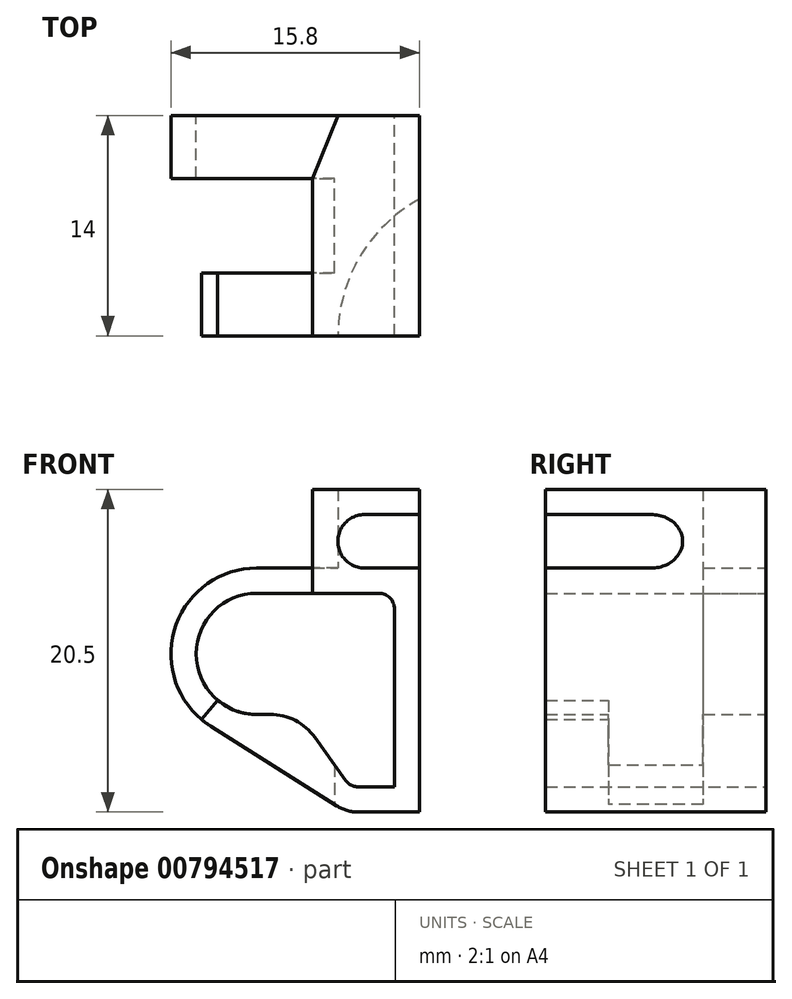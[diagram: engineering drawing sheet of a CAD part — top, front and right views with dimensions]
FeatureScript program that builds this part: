
annotation { "Feature Type Name" : "Feature", "Feature Type Description" : "" }
export const myFeature = defineFeature(function(context is Context, id is Id, definition is map)
    precondition{}
    {
        {
            var Q0;
            Q0=qCreatedBy(makeId("Front.planeOp"),FACE);
            var sketch = newSketch(context, id + "F0", { "sketchPlane" : qUnion([Q0])});
            skLineSegment(sketch, "E0", {"start": v(0, -12.3) * mm, "end": v(0, -1) * mm});
            skLineSegment(sketch, "E1", {"start": v(-1, 0) * mm, "end": v(-8.75, 0) * mm});
            skLineSegment(sketch, "E2", {"start": v(0, -12.3) * mm, "end": v(-2.29, -12.3) * mm});
            skLineSegment(sketch, "E3", {"start": v(-3.1, -11.88) * mm, "end": v(-5.05, -9.16) * mm});
            skLineSegment(sketch, "E4", {"start": v(-7.9, -7.7) * mm, "end": v(-8.75, -7.7) * mm});
            skArc(sketch, "E5", {"start": v(-8.75, 0) * mm, "mid": v(-12.6, -3.85) * mm, "end": v(-8.75, -7.7) * mm});
            skPoint(sketch, "E6.visualSharp", {"position": v(-6.1, -7.7) * mm});
            skArc(sketch, "E6.filletArc", {"start": v(-5.05, -9.16) * mm, "mid": v(-6.3, -8.09) * mm, "end": v(-7.9, -7.7) * mm});
            skPoint(sketch, "E7.visualSharp", {"position": v(-2.8, -12.3) * mm});
            skArc(sketch, "E7.filletArc", {"start": v(-3.1, -11.88) * mm, "mid": v(-2.74, -12.19) * mm, "end": v(-2.29, -12.3) * mm});
            skPoint(sketch, "E8.visualSharp", {"position": v(0, 0) * mm});
            skArc(sketch, "E8.filletArc", {"start": v(0, -1) * mm, "mid": v(-0.3, -0.3) * mm, "end": v(-1, 0) * mm});
            skLineSegment(sketch, "E9.1", {"start": v(1.6, -13.9) * mm, "end": v(1.6, 1.6) * mm});
            skArc(sketch, "E9.2", {"start": v(-8.75, 1.6) * mm, "mid": v(-13.99, -2.34) * mm, "end": v(-11.66, -8.46) * mm});
            skArc(sketch, "E9.4", {"start": v(-3.67, -13.5) * mm, "mid": v(-3, -13.8) * mm, "end": v(-2.29, -13.9) * mm});
            skLineSegment(sketch, "E9.5", {"start": v(1.6, 1.6) * mm, "end": v(-8.75, 1.6) * mm});
            skLineSegment(sketch, "E9.6", {"start": v(1.6, -13.9) * mm, "end": v(-2.29, -13.9) * mm});
            skLineSegment(sketch, "E10", {"start": v(-11.66, -8.46) * mm, "end": v(-3.67, -13.5) * mm});
            skSolve(sketch);
        }
        {
            var Q0;
            Q0=makeQuery(id+"F0.imprint","IMPRINT",FACE,{"disambiguationData":[TD([[makeQuery(id+"F0.imprint","IMPRINT",EDGE,{"derivedFrom":sQuery(id+"F0.wireOp",EDGE,"E0")}),-1.0]])]});
            extrude(context, id + "F1", {"entities" : qUnion([Q0]), "depth" : 14 * mm, "offsetDistance" : 25 * mm});
        }
        {
            var Q0;
            Q0=makeQuery(id+"F1.opExtrude","CAP_FACE",FACE,{"disambiguationData":[OSD([sQuery(id+"F0.wireOp",EDGE,"E0"),sQuery(id+"F0.wireOp",EDGE,"E1"),sQuery(id+"F0.wireOp",EDGE,"E2"),sQuery(id+"F0.wireOp",EDGE,"E3"),sQuery(id+"F0.wireOp",EDGE,"E4"),sQuery(id+"F0.wireOp",EDGE,"E5"),sQuery(id+"F0.wireOp",EDGE,"E6.filletArc"),sQuery(id+"F0.wireOp",EDGE,"E7.filletArc"),sQuery(id+"F0.wireOp",EDGE,"E8.filletArc"),sQuery(id+"F0.wireOp",EDGE,"E9.0"),sQuery(id+"F0.wireOp",EDGE,"E9.1"),sQuery(id+"F0.wireOp",EDGE,"E9.2"),sQuery(id+"F0.wireOp",EDGE,"E9.4"),sQuery(id+"F0.wireOp",EDGE,"E9.5"),sQuery(id+"F0.wireOp",EDGE,"E9.6"),sQuery(id+"F0.wireOp",EDGE,"E10")])],"isStart":false});
            var sketch = newSketch(context, id + "F2", { "sketchPlane" : qUnion([Q0])});
            skLineSegment(sketch, "E11", {"start": v(-5.2, 8.6) * mm, "end": v(-5.2, -3.4) * mm});
            skLineSegment(sketch, "E12", {"start": v(-5.2, -3.4) * mm, "end": v(-3.8, -3.4) * mm});
            skLineSegment(sketch, "E13", {"start": v(-3.8, -3.4) * mm, "end": v(-3.8, -16.4) * mm});
            skLineSegment(sketch, "E14", {"start": v(-3.8, -16.4) * mm, "end": v(-19.2, -16.4) * mm});
            skLineSegment(sketch, "E15", {"start": v(-19.2, -16.4) * mm, "end": v(-19.2, 8.6) * mm});
            skLineSegment(sketch, "E16", {"start": v(-19.2, 8.6) * mm, "end": v(-5.2, 8.6) * mm});
            skSolve(sketch);
        }
        {
            var Q0;
            {var subQ1=sQuery(id+"F2.wireOp",EDGE,"E14");Q0=makeQuery(id+"F2.imprint","IMPRINT",FACE,{"disambiguationData":[TD([[makeQuery(id+"F2.imprint","IMPRINT",EDGE,{"derivedFrom":subQ1}),-1.0]])]});}
            var Q1;
            {var subQ1=sQuery(id+"F2.wireOp",EDGE,"E12");Q1=makeQuery(id+"F2.imprint","IMPRINT",FACE,{"disambiguationData":[TD([[makeQuery(id+"F2.imprint","IMPRINT",EDGE,{"derivedFrom":subQ1}),-1.0]])]});}
            var Q2;
            {var subQ3=makeQuery(id+"F1.opExtrude","CAP_EDGE",EDGE,{"disambiguationData":[OSD([sQuery(id+"F0.wireOp",EDGE,"E3")])],"isStart":false});Q2=makeQuery(id+"F2.imprint","IMPRINT",FACE,{"disambiguationData":[TD([[makeQuery(id+"F2.imprint","IMPRINT",EDGE,{"derivedFrom":subQ3}),1.0]])]});}
            extrude(context, id + "F3", {"entities" : qUnion([Q0, Q1, Q2]), "operationType" : NewBodyOperationType.REMOVE, "oppositeDirection" : true, "depth" : 10 * mm, "offsetDistance" : 25 * mm, "hasSecondDirection" : true, "secondDirectionOppositeDirection" : true, "secondDirectionDepth" : 4 * mm});
        }
        {
            var Q0;
            Q0=makeQuery(id+"F1.opExtrude","SWEPT_FACE",FACE,{"disambiguationData":[OSD([sQuery(id+"F0.wireOp",EDGE,"E1")])]});
            var sketch = newSketch(context, id + "F4", { "sketchPlane" : qUnion([Q0])});
            skCircle(sketch, "E17", {"center": v(-2, 7) * mm, "radius": 1.25 * mm});
            skSolve(sketch);
        }
        {
            var Q0;
            Q0=makeQuery(id+"F2.imprint","IMPRINT",FACE,{"disambiguationData":[TD([[makeQuery(id+"F2.imprint","IMPRINT",EDGE,{"derivedFrom":makeQuery(id+"F1.opExtrude","CAP_EDGE",EDGE,{"disambiguationData":[OSD([sQuery(id+"F0.wireOp",EDGE,"E4")])],"isStart":false})}),1.0]])]});
            var sketch = newSketch(context, id + "F5", { "sketchPlane" : qUnion([Q0])});
            skLineSegment(sketch, "E18.0", {"start": v(-19.2, 8.6) * mm, "end": v(-5.2, 8.6) * mm});
            skLineSegment(sketch, "E19.0", {"start": v(-5.2, 8.6) * mm, "end": v(-5.2, -3.85) * mm});
            skLineSegment(sketch, "E20.0", {"start": v(-19.2, -16.3) * mm, "end": v(-19.2, 8.6) * mm});
            skLineSegment(sketch, "E21", {"start": v(-8.75, -3.85) * mm, "end": v(-5.2, -3.85) * mm});
            skLineSegment(sketch, "E22", {"start": v(-8.75, -3.85) * mm, "end": v(-19.2, -16.3) * mm});
            skPoint(sketch, "E23.orphan", {"position": v(-5.2, -3.4) * mm});
            skPoint(sketch, "E24.orphan", {"position": v(-19.2, -16.4) * mm});
            skSolve(sketch);
        }
        {
            var Q0;
            Q0 = qSketchRegion(id + "F5", true);
            extrude(context, id + "F6", {"entities" : qUnion([Q0]), "operationType" : NewBodyOperationType.REMOVE, "oppositeDirection" : true, "depth" : 4.1 * mm, "offsetDistance" : 25 * mm});
        }
        {
            var Q0;
            Q0=makeQuery(id+"F1.opExtrude","SWEPT_FACE",FACE,{"disambiguationData":[OSD([sQuery(id+"F0.wireOp",EDGE,"E9.1")])]});
            var sketch = newSketch(context, id + "F7", { "sketchPlane" : qUnion([Q0])});
            skLineSegment(sketch, "E25.bottom", {"start": v(-14, -6.2) * mm, "end": v(0, -6.2) * mm});
            skLineSegment(sketch, "E25.top", {"start": v(-14, -7.4) * mm, "end": v(0, -7.4) * mm});
            skLineSegment(sketch, "E25.left", {"start": v(-14, -6.2) * mm, "end": v(-14, -7.4) * mm});
            skLineSegment(sketch, "E25.right", {"start": v(0, -6.2) * mm, "end": v(0, -7.4) * mm});
            skSolve(sketch);
        }
        {
            var Q0;
            Q0=makeQuery(id+"F1.opExtrude","SWEPT_FACE",FACE,{"disambiguationData":[OSD([sQuery(id+"F0.wireOp",EDGE,"E9.5")])]});
            var sketch = newSketch(context, id + "F8", { "sketchPlane" : qUnion([Q0])});
            skLineSegment(sketch, "E26", {"start": v(-5.2, -14) * mm, "end": v(-5.2, -4) * mm});
            skLineSegment(sketch, "E27", {"start": v(1.6, 0) * mm, "end": v(1.6, -14) * mm});
            skLineSegment(sketch, "E28", {"start": v(1.6, -14) * mm, "end": v(-5.2, -14) * mm});
            skLineSegment(sketch, "E29", {"start": v(-5.2, -4) * mm, "end": v(-3.58, 0) * mm});
            skLineSegment(sketch, "E30", {"start": v(-3.58, 0) * mm, "end": v(1.6, 0) * mm});
            skSolve(sketch);
        }
        {
            var Q0;
            Q0 = qSketchRegion(id + "F8", true);
            extrude(context, id + "F9", {"entities" : qUnion([Q0]), "operationType" : NewBodyOperationType.ADD, "depth" : 5 * mm, "offsetDistance" : 25 * mm});
        }
        {
            var Q0;
            Q0=makeQuery(id+"F1.opExtrude","SWEPT_FACE",FACE,{"disambiguationData":[OSD([sQuery(id+"F0.wireOp",EDGE,"E1")])]});
            var Q1;
            Q1=makeQuery(id+"F9.opExtrude","CAP_FACE",FACE,{"disambiguationData":[OSD([sQuery(id+"F8.wireOp",EDGE,"E26"),sQuery(id+"F8.wireOp",EDGE,"E27"),sQuery(id+"F8.wireOp",EDGE,"E28"),sQuery(id+"F8.wireOp",EDGE,"E29"),sQuery(id+"F8.wireOp",EDGE,"E30")])],"isStart":false});
            cPlane(context, id + "F10", {"entities" : qUnion([Q0, Q1]), "cplaneType" : CPlaneType.MID_PLANE, "offset" : 25 * mm, "width" : 150 * mm, "height" : 150 * mm});
        }
        {
            var Q0;
            Q0=qCreatedBy(id+"F10.planeOp",FACE);
            var sketch = newSketch(context, id + "F11", { "sketchPlane" : qUnion([Q0])});
            skLineSegment(sketch, "E31", {"start": v(1.6, 7) * mm, "end": v(-7.21, 7) * mm, "construction": true});
            skLineSegment(sketch, "E32", {"start": v(-3.6, 14) * mm, "end": v(1.6, 14) * mm});
            skLineSegment(sketch, "E33", {"start": v(1.6, 5.3) * mm, "end": v(1.6, 14) * mm});
            skArc(sketch, "E34", {"start": v(-3.6, 14) * mm, "mid": v(-2.18, 8.94) * mm, "end": v(1.6, 5.3) * mm});
            skSolve(sketch);
        }
        {
            var Q0;
            Q0 = qSketchRegion(id + "F11", true);
            extrude(context, id + "F12", {"entities" : qUnion([Q0]), "operationType" : NewBodyOperationType.REMOVE, "endBound" : BoundingType.SYMMETRIC, "oppositeDirection" : true, "depth" : 3.4 * mm, "offsetDistance" : 25 * mm});
        }
        {
            var Q0;
            Q0=makeQuery(id+"F12.boolean.opBoolean","COPY",EDGE,{"derivedFrom":makeQuery(id+"F12.opExtrude","CAP_EDGE",EDGE,{"disambiguationData":[OSD([sQuery(id+"F11.wireOp",EDGE,"E34")])],"isStart":false})});
            var Q1;
            Q1=makeQuery(id+"F12.boolean.opBoolean","COPY",EDGE,{"derivedFrom":makeQuery(id+"F12.opExtrude","CAP_EDGE",EDGE,{"disambiguationData":[OSD([sQuery(id+"F11.wireOp",EDGE,"E34")])],"isStart":true})});
            fillet(context, id + "F13", {"entities" : qUnion([Q0, Q1]), "radius" : 1.7 * mm, "tangentPropagation" : true, "allowEdgeOverflow" : false});
        }
    });
